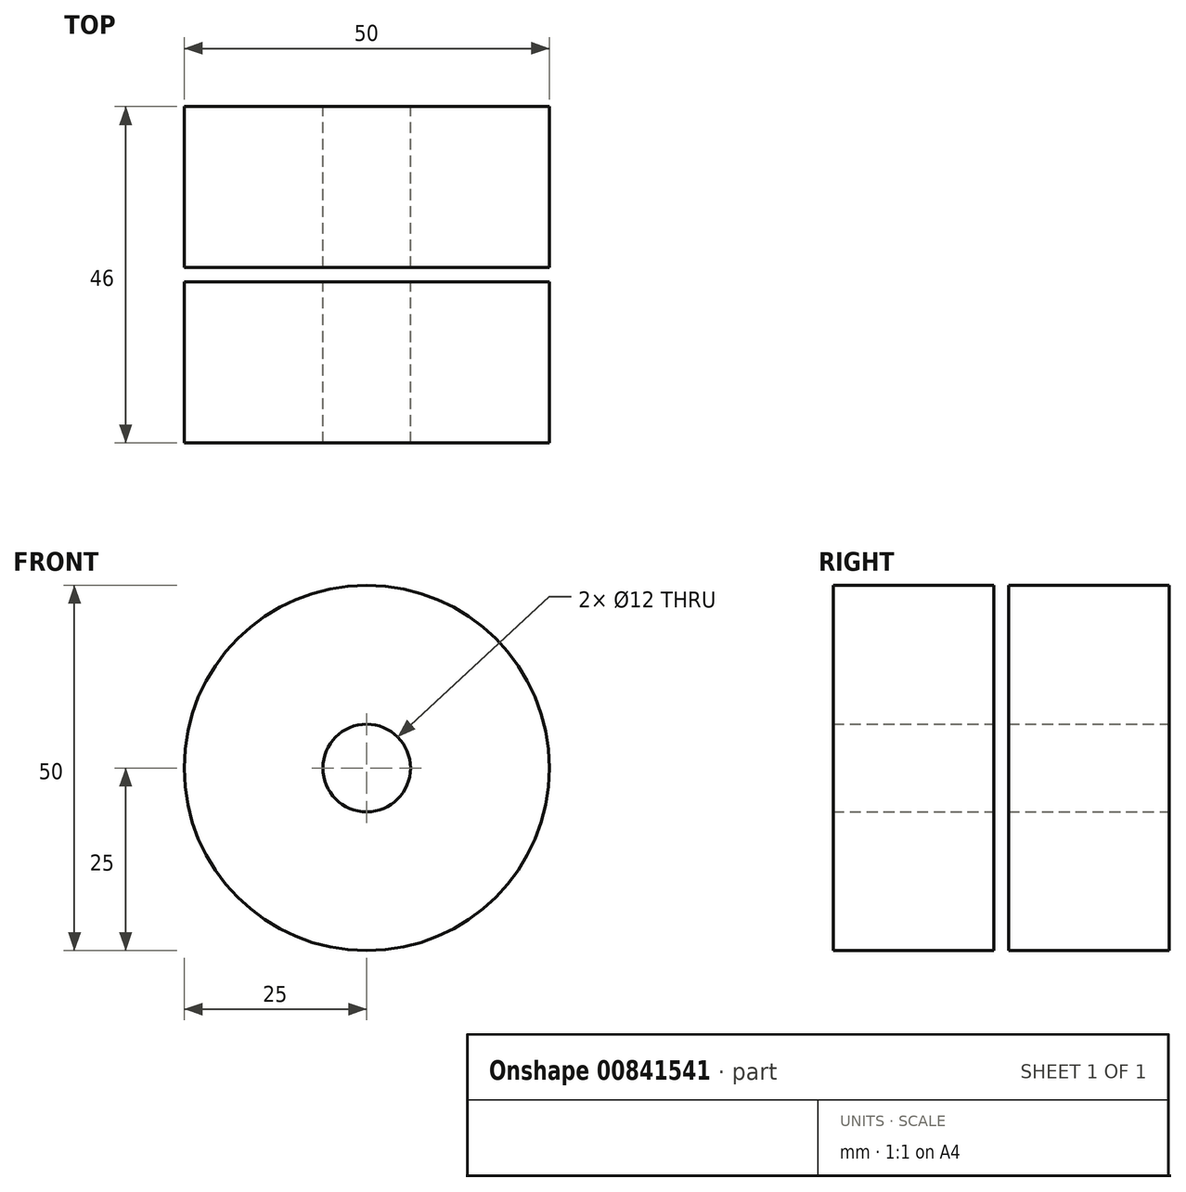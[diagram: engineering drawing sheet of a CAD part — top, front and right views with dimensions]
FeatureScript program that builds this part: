
annotation { "Feature Type Name" : "Feature", "Feature Type Description" : "" }
export const myFeature = defineFeature(function(context is Context, id is Id, definition is map)
    precondition{}
    {
        {
            var Q0;
            Q0=qCreatedBy(makeId("Front.planeOp"),FACE);
            var sketch = newSketch(context, id + "F0", { "sketchPlane" : qUnion([Q0])});
            skCircle(sketch, "E0", {"center": v(0, 0) * mm, "radius": 25 * mm});
            skCircle(sketch, "E1", {"center": v(0, 0) * mm, "radius": 6 * mm});
            skSolve(sketch);
        }
        {
            var Q0;
            Q0=makeQuery(id+"F0.imprint","IMPRINT",FACE,{"disambiguationData":[TD([[makeQuery(id+"F0.imprint","IMPRINT",EDGE,{"derivedFrom":sQuery(id+"F0.wireOp",EDGE,"E0")}),1.0]])]});
            extrude(context, id + "F1", {"entities" : qUnion([Q0]), "depth" : 22 * mm, "offsetDistance" : 25 * mm, "hasSecondDirection" : true, "secondDirectionOppositeDirection" : true, "secondDirectionDepth" : 24 * mm});
        }
        {
            var Q0;
            Q0=makeQuery(id+"F0.imprint","IMPRINT",FACE,{"disambiguationData":[TD([[makeQuery(id+"F0.imprint","IMPRINT",EDGE,{"derivedFrom":sQuery(id+"F0.wireOp",EDGE,"E0")}),1.0]])]});
            extrude(context, id + "F2", {"entities" : qUnion([Q0]), "operationType" : NewBodyOperationType.REMOVE, "oppositeDirection" : true, "depth" : 2 * mm, "offsetDistance" : 25 * mm});
        }
    });
